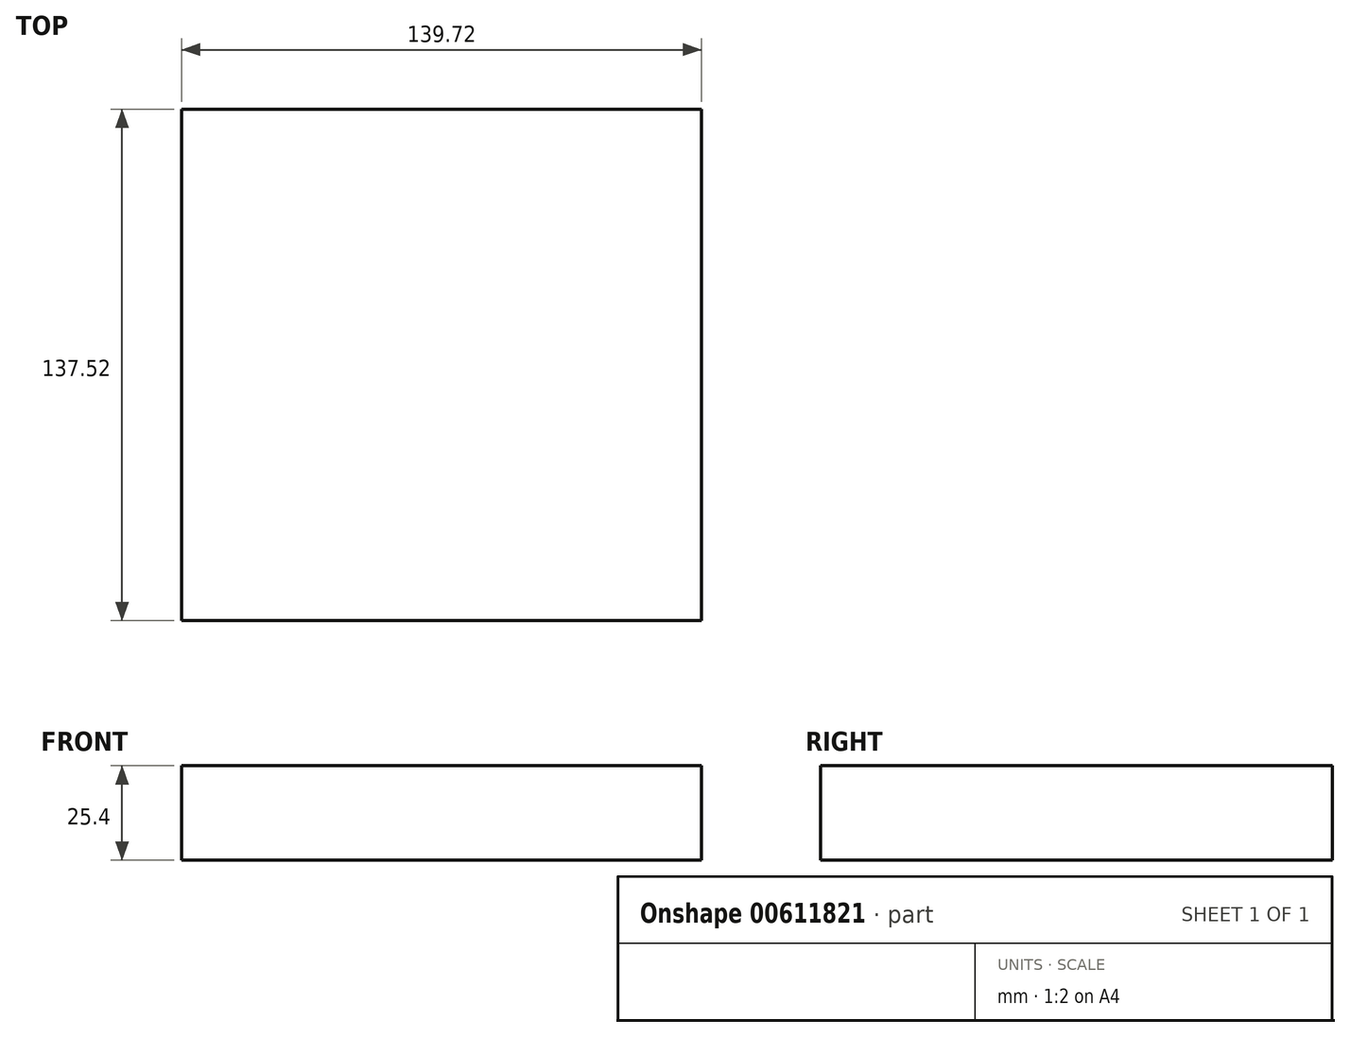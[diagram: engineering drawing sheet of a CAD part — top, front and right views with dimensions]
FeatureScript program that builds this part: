
annotation { "Feature Type Name" : "Feature", "Feature Type Description" : "" }
export const myFeature = defineFeature(function(context is Context, id is Id, definition is map)
    precondition{}
    {
        {
            var Q0;
            Q0=qCreatedBy(makeId("Top.planeOp"),FACE);
            var sketch = newSketch(context, id + "F0", { "sketchPlane" : qUnion([Q0])});
            skLineSegment(sketch, "E0.bottom", {"start": v(69.86, -68.76) * mm, "end": v(-69.86, -68.76) * mm});
            skLineSegment(sketch, "E0.top", {"start": v(69.86, 68.76) * mm, "end": v(-69.86, 68.76) * mm});
            skLineSegment(sketch, "E0.left", {"start": v(69.86, -68.76) * mm, "end": v(69.86, 68.76) * mm});
            skLineSegment(sketch, "E0.right", {"start": v(-69.86, -68.76) * mm, "end": v(-69.86, 68.76) * mm});
            skPoint(sketch, "E0.middle", {"position": v(0, 0) * mm});
            skLineSegment(sketch, "E1", {"start": v(0, 68.76) * mm, "end": v(0, -68.76) * mm});
            skSolve(sketch);
        }
        {
            var Q0;
            {var subQ0=sQuery(id+"F0.wireOp",EDGE,"E0.left");Q0=makeQuery(id+"F0.imprint","IMPRINT",FACE,{"disambiguationData":[TD([[makeQuery(id+"F0.imprint","IMPRINT",EDGE,{"derivedFrom":subQ0}),1.0]])]});}
            var Q1;
            {var subQ0=sQuery(id+"F0.wireOp",EDGE,"E0.right");Q1=makeQuery(id+"F0.imprint","IMPRINT",FACE,{"disambiguationData":[TD([[makeQuery(id+"F0.imprint","IMPRINT",EDGE,{"derivedFrom":subQ0}),-1.0]])]});}
            extrude(context, id + "F1", {"entities" : qUnion([Q0, Q1]), "depth" : 25.4 * mm, "offsetDistance" : 25.4 * mm});
        }
    });
